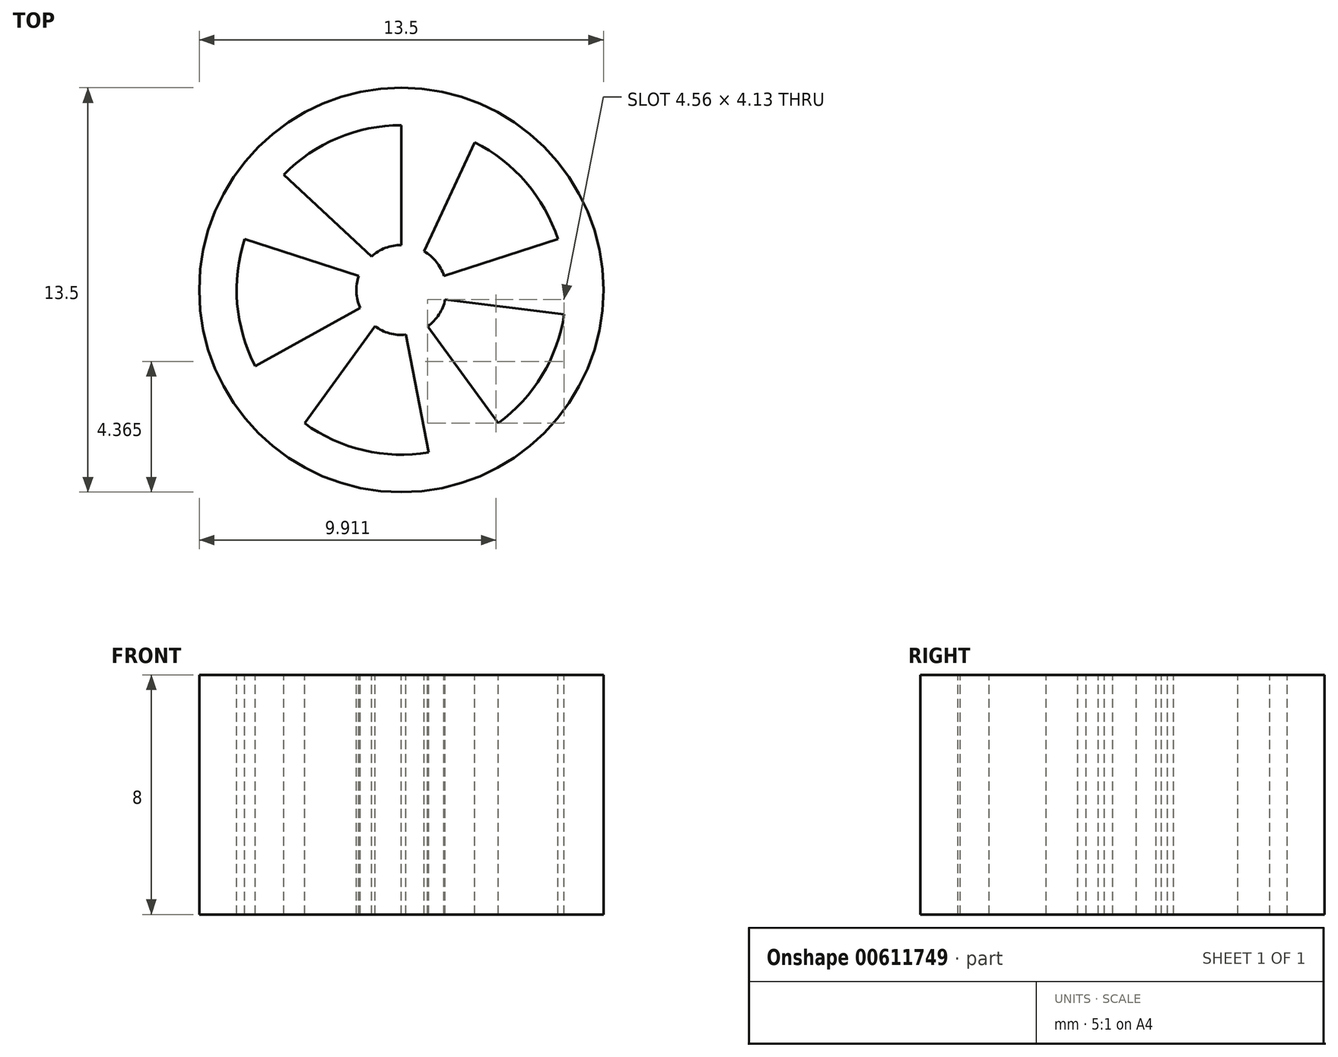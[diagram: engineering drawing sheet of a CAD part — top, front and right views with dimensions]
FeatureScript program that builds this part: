
annotation { "Feature Type Name" : "Feature", "Feature Type Description" : "" }
export const myFeature = defineFeature(function(context is Context, id is Id, definition is map)
    precondition{}
    {
        {
            var Q0;
            Q0=qCreatedBy(makeId("Top.planeOp"),FACE);
            var sketch = newSketch(context, id + "F0", { "sketchPlane" : qUnion([Q0])});
            skCircle(sketch, "E0", {"center": v(0, 0) * mm, "radius": 6.75 * mm});
            skSolve(sketch);
        }
        {
            var Q0;
            Q0 = qSketchRegion(id + "F0", true);
            extrude(context, id + "F1", {"entities" : qUnion([Q0]), "depth" : 8 * mm, "offsetDistance" : 25 * mm});
        }
        {
            var Q0;
            Q0=makeQuery(id+"F1.opExtrude","CAP_FACE",FACE,{"disambiguationData":[OSD([sQuery(id+"F0.wireOp",EDGE,"E0")])],"isStart":false});
            var sketch = newSketch(context, id + "F2", { "sketchPlane" : qUnion([Q0])});
            skCircle(sketch, "E1", {"center": v(0, 0) * mm, "radius": 5.5 * mm});
            skCircle(sketch, "E2", {"center": v(0, 0) * mm, "radius": 1.5 * mm});
            skLineSegment(sketch, "E3", {"start": v(0, 1.5) * mm, "end": v(0, 5.5) * mm});
            skLineSegment(sketch, "E4", {"start": v(0.76, 1.3) * mm, "end": v(2.45, 4.92) * mm});
            skLineSegment(sketch, "E5.1.0", {"start": v(-1.43, 0.46) * mm, "end": v(-5.23, 1.7) * mm});
            skLineSegment(sketch, "E5.1.1", {"start": v(-1, 1.12) * mm, "end": v(-3.93, 3.85) * mm});
            skLineSegment(sketch, "E5.2.0", {"start": v(-0.88, -1.21) * mm, "end": v(-3.23, -4.45) * mm});
            skLineSegment(sketch, "E5.2.1", {"start": v(-1.37, -0.6) * mm, "end": v(-4.88, -2.54) * mm});
            skLineSegment(sketch, "E5.3.0", {"start": v(0.88, -1.21) * mm, "end": v(3.23, -4.45) * mm});
            skLineSegment(sketch, "E5.3.1", {"start": v(0.15, -1.5) * mm, "end": v(0.91, -5.42) * mm});
            skLineSegment(sketch, "E5.4.0", {"start": v(1.43, 0.46) * mm, "end": v(5.23, 1.7) * mm});
            skLineSegment(sketch, "E5.4.1", {"start": v(1.47, -0.32) * mm, "end": v(5.44, -0.8) * mm});
            skSolve(sketch);
        }
        {
            var Q0;
            {var subQ0=sQuery(id+"F2.wireOp",EDGE,"E3");Q0=makeQuery(id+"F2.imprint","IMPRINT",FACE,{"disambiguationData":[TD([[makeQuery(id+"F2.imprint","IMPRINT",EDGE,{"derivedFrom":subQ0}),1.0]])]});}
            var Q1;
            {var subQ0=sQuery(id+"F2.wireOp",EDGE,"E5.1.0");Q1=makeQuery(id+"F2.imprint","IMPRINT",FACE,{"disambiguationData":[TD([[makeQuery(id+"F2.imprint","IMPRINT",EDGE,{"derivedFrom":subQ0}),1.0]])]});}
            var Q2;
            {var subQ0=sQuery(id+"F2.wireOp",EDGE,"E5.2.0");Q2=makeQuery(id+"F2.imprint","IMPRINT",FACE,{"disambiguationData":[TD([[makeQuery(id+"F2.imprint","IMPRINT",EDGE,{"derivedFrom":subQ0}),1.0]])]});}
            var Q3;
            {var subQ0=sQuery(id+"F2.wireOp",EDGE,"E5.3.0");Q3=makeQuery(id+"F2.imprint","IMPRINT",FACE,{"disambiguationData":[TD([[makeQuery(id+"F2.imprint","IMPRINT",EDGE,{"derivedFrom":subQ0}),1.0]])]});}
            var Q4;
            {var subQ0=sQuery(id+"F2.wireOp",EDGE,"E4");Q4=makeQuery(id+"F2.imprint","IMPRINT",FACE,{"disambiguationData":[TD([[makeQuery(id+"F2.imprint","IMPRINT",EDGE,{"derivedFrom":subQ0}),-1.0]])]});}
            extrude(context, id + "F3", {"entities" : qUnion([Q0, Q1, Q2, Q3, Q4]), "operationType" : NewBodyOperationType.REMOVE, "oppositeDirection" : true, "depth" : 8 * mm, "offsetDistance" : 25 * mm});
        }
    });
